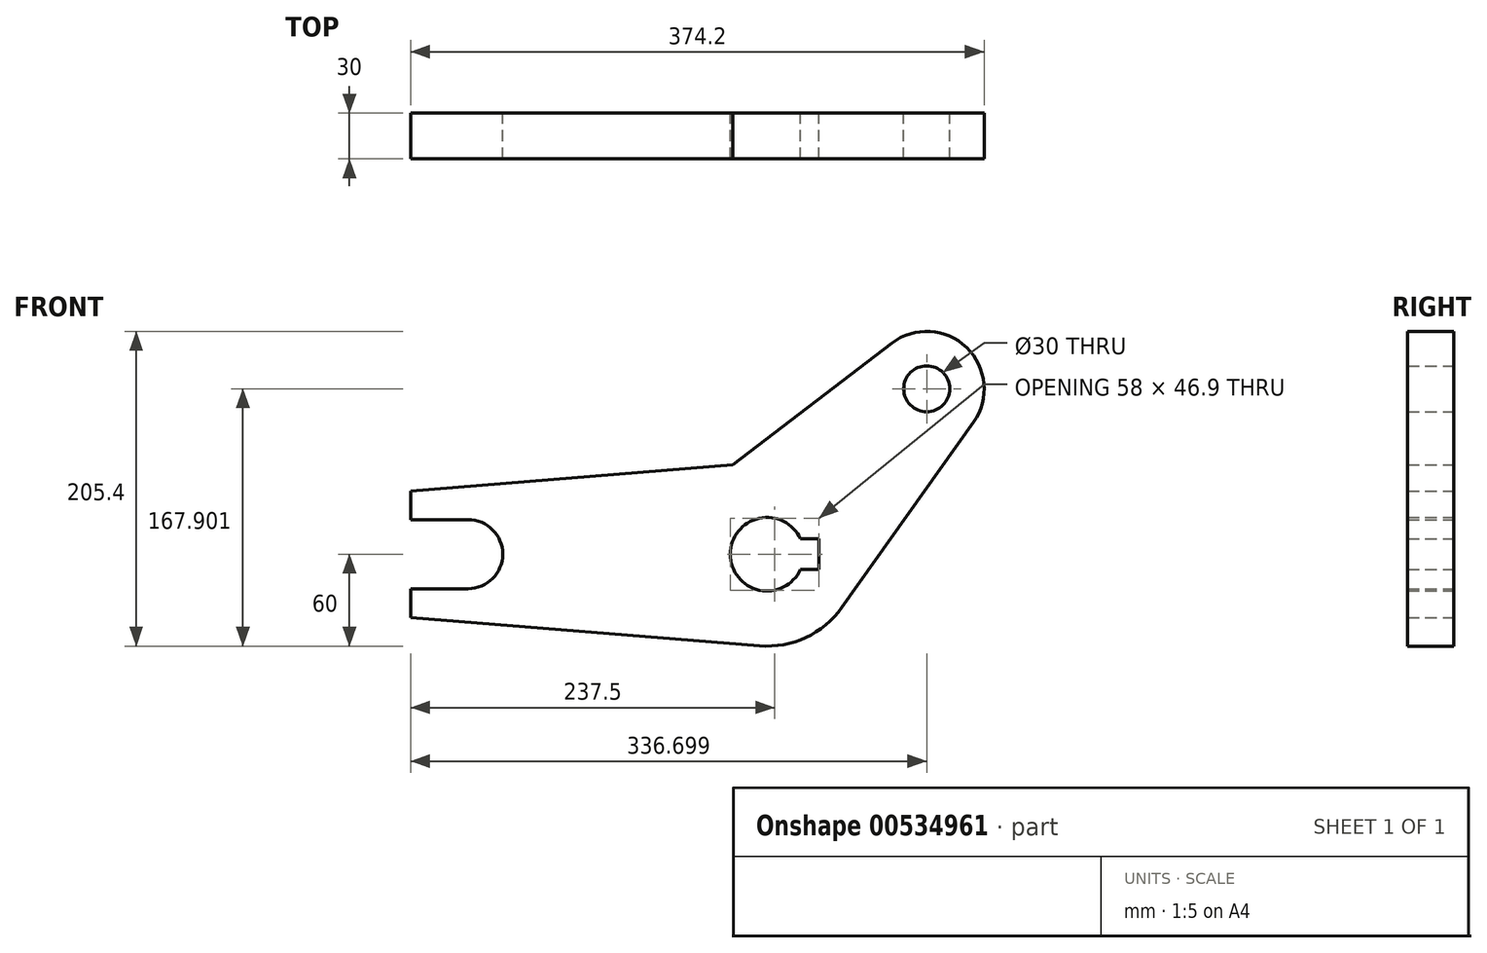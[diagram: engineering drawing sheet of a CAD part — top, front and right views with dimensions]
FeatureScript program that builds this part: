
annotation { "Feature Type Name" : "Feature", "Feature Type Description" : "" }
export const myFeature = defineFeature(function(context is Context, id is Id, definition is map)
    precondition{}
    {
        {
            var Q0;
            Q0=qCreatedBy(makeId("Front.planeOp"),FACE);
            var sketch = newSketch(context, id + "F0", { "sketchPlane" : qUnion([Q0])});
            skCircle(sketch, "E0", {"center": v(0, 0) * mm, "radius": 60 * mm});
            skCircle(sketch, "E1", {"center": v(104.2, 107.9) * mm, "radius": 15 * mm});
            skCircle(sketch, "E2", {"center": v(104.2, 107.9) * mm, "radius": 37.5 * mm});
            skLineSegment(sketch, "E3", {"start": v(81.44, 137.7) * mm, "end": v(-36.42, 47.68) * mm});
            skLineSegment(sketch, "E4", {"start": v(134.78, 86.2) * mm, "end": v(48.92, -34.73) * mm});
            skLineSegment(sketch, "E5", {"start": v(-4.86, 59.8) * mm, "end": v(-232.5, 41.31) * mm});
            skLineSegment(sketch, "E6", {"start": v(-232.5, 41.31) * mm, "end": v(-232.5, 22.5) * mm});
            skLineSegment(sketch, "E7", {"start": v(-232.5, 22.5) * mm, "end": v(-195, 22.5) * mm});
            skLineSegment(sketch, "E8", {"start": v(-4.86, -59.8) * mm, "end": v(-232.5, -41.3) * mm});
            skLineSegment(sketch, "E9", {"start": v(-232.5, -41.3) * mm, "end": v(-232.5, -22.5) * mm});
            skLineSegment(sketch, "E10", {"start": v(-232.5, -22.5) * mm, "end": v(-195, -22.5) * mm});
            skArc(sketch, "E11", {"start": v(-195, -22.5) * mm, "mid": v(-172.5, 0) * mm, "end": v(-195, 22.5) * mm});
            skPoint(sketch, "E12", {"position": v(-60, 0) * mm});
            skLineSegment(sketch, "E13", {"start": v(-172.5, 0) * mm, "end": v(-60, 0) * mm});
            skLineSegment(sketch, "E14", {"start": v(0, 0) * mm, "end": v(104.2, 107.9) * mm});
            skArc(sketch, "E15", {"start": v(21.82, 10) * mm, "mid": v(-24, 0) * mm, "end": v(21.82, -10) * mm});
            skLineSegment(sketch, "E16", {"start": v(21.82, 10) * mm, "end": v(34, 10) * mm});
            skLineSegment(sketch, "E17", {"start": v(34, 10) * mm, "end": v(34, -10) * mm});
            skLineSegment(sketch, "E18", {"start": v(34, -10) * mm, "end": v(21.82, -10) * mm});
            skPoint(sketch, "E19", {"position": v(21.82, 10) * mm});
            skPoint(sketch, "E20", {"position": v(21.82, -10) * mm});
            skLineSegment(sketch, "E21", {"start": v(0, 0) * mm, "end": v(34, 0) * mm, "construction": true});
            skSolve(sketch);
        }
        {
            var Q0;
            Q0 = qSketchRegion(id + "F0", true);
            extrude(context, id + "F1", {"entities" : qUnion([Q0]), "depth" : 30 * mm, "offsetDistance" : 25 * mm});
        }
    });
